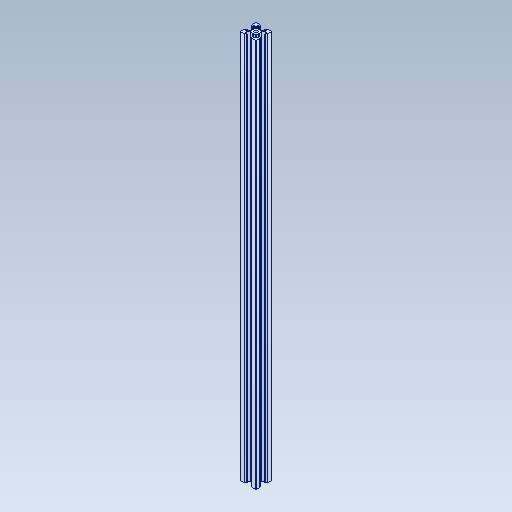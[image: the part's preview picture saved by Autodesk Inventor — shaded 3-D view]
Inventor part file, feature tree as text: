
AUTODESK INVENTOR PART (.ipt)
format: ipt  version: 2021 (Build 250183000, 183)  size: 219,136 bytes
history: native  units: mm
features: sketch x3, extrude x2, fillet x2, other x1, pattern_circular x1, hole x1, projected_geometry x1
ambient origin geometry x8: Origin, YZ Plane, XZ Plane, XY Plane, X Axis, Y Axis, Z Axis, Center Point
bodies: Body1 (feature_tree)
feature tree (11):
  other  "實體1"
  extrude  "擠出1"  Depth=20.0mm
  extrude  "擠出2"  Depth=20.0mm
  fillet  "圓角1"  Radius=500.0mm
  pattern_circular  "環形陣列1"  [2 undecoded]
  hole  "孔1"  [1 undecoded]
  fillet  "圓角2"  Radius=6.2mm
  sketch  "草圖1"
  sketch  "草圖2"
  projected_geometry  "投影迴路1"
  sketch  "草圖3"
note: 3 required parameter values undecoded (feature->parameter linkage not recoverable at this tier; creation-order binding heuristic only, values carry confidence <= 0.55)
